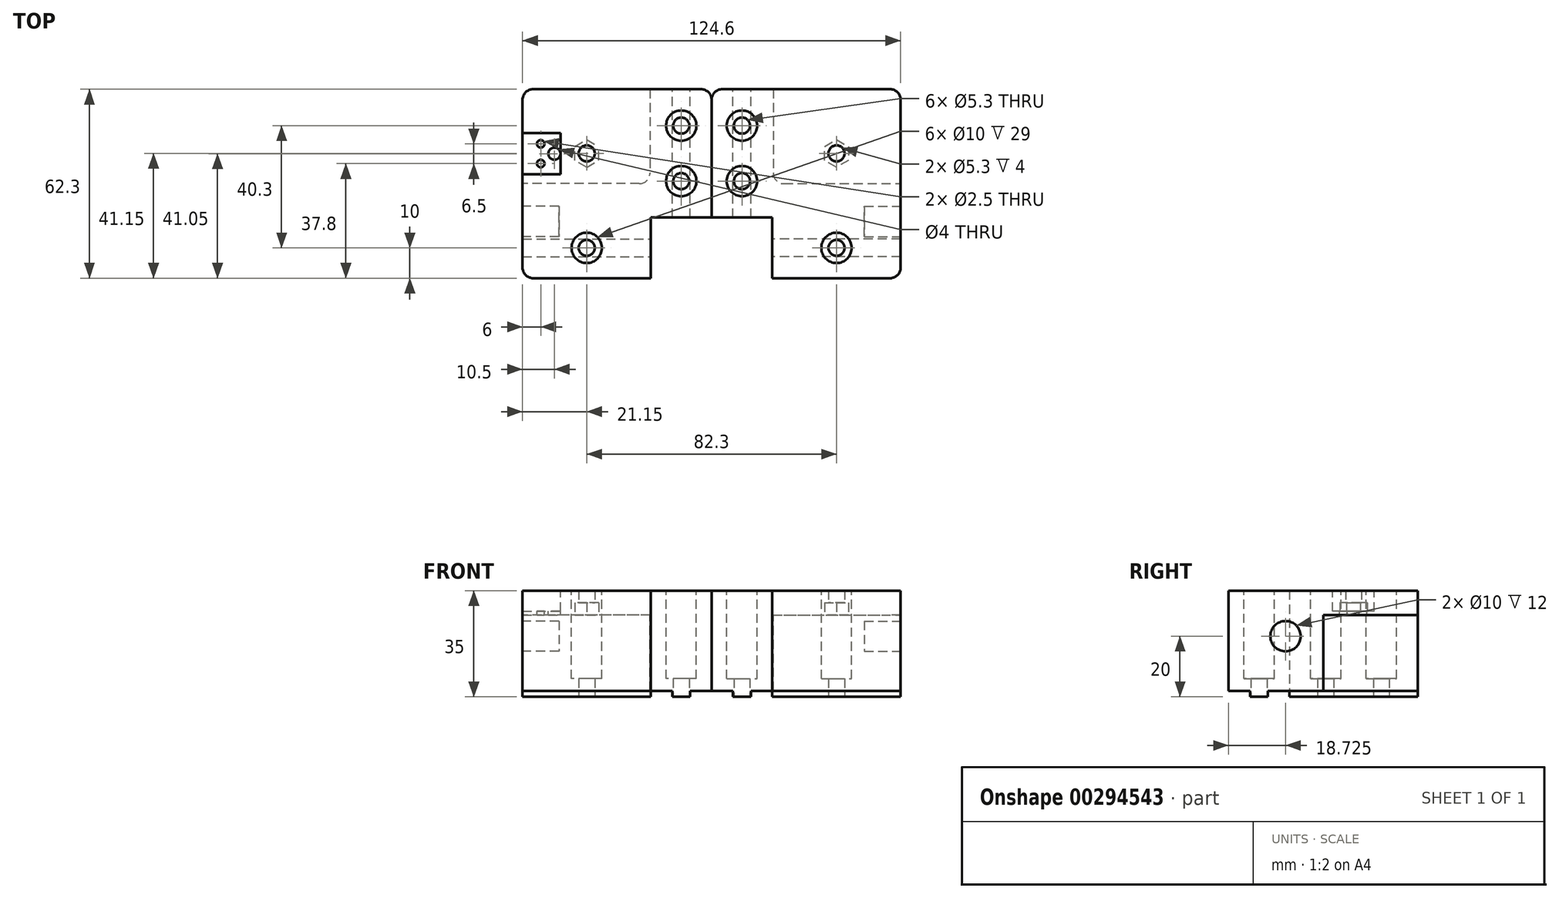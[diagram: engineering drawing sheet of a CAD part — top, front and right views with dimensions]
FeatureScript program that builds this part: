
annotation { "Feature Type Name" : "Feature", "Feature Type Description" : "" }
export const myFeature = defineFeature(function(context is Context, id is Id, definition is map)
    precondition{}
    {
        {
            var Q0;
            Q0=qCreatedBy(makeId("Top.planeOp"),FACE);
            var sketch = newSketch(context, id + "F0", { "sketchPlane" : qUnion([Q0])});
            skLineSegment(sketch, "E0.bottom", {"start": v(-21.15, 35) * mm, "end": v(41.15, 35) * mm});
            skLineSegment(sketch, "E0.top", {"start": v(-21.15, -27.3) * mm, "end": v(21.15, -27.3) * mm});
            skLineSegment(sketch, "E0.left", {"start": v(-21.15, 35) * mm, "end": v(-21.15, -27.3) * mm});
            skLineSegment(sketch, "E0.right", {"start": v(41.15, 35) * mm, "end": v(41.15, -7.3) * mm});
            skLineSegment(sketch, "E1.top", {"start": v(41.15, -7.3) * mm, "end": v(21.15, -7.3) * mm});
            skLineSegment(sketch, "E1.right", {"start": v(21.15, -27.3) * mm, "end": v(21.15, -7.3) * mm});
            skCircle(sketch, "E2", {"center": v(31.15, 23) * mm, "radius": 2.65 * mm});
            skCircle(sketch, "E3", {"center": v(31.15, 4.7) * mm, "radius": 2.65 * mm});
            skCircle(sketch, "E4", {"center": v(0, -17.3) * mm, "radius": 2.65 * mm});
            skPoint(sketch, "E4.centerSnap0", {"position": v(0, -27.3) * mm});
            skCircle(sketch, "E5", {"center": v(0, 13.85) * mm, "radius": 2.65 * mm});
            skSolve(sketch);
        }
        {
            var Q0;
            Q0=qSketchRegion(id+"F0",true);
            extrude(context, id + "F1", {"entities" : qUnion([Q0]), "depth" : 33 * mm});
        }
        {
            var Q0;
            Q0=makeQuery(id+"F1.opExtrude","SWEPT_FACE",FACE,{"disambiguationData":[OSD([sQuery(id+"F0.wireOp",EDGE,"E0.left")])]});
            var sketch = newSketch(context, id + "F2", { "sketchPlane" : qUnion([Q0])});
            skCircle(sketch, "E6", {"center": v(8.58, 18) * mm, "radius": 5 * mm});
            skSolve(sketch);
        }
        {
            var Q0;
            Q0=qSketchRegion(id+"F2",true);
            extrude(context, id + "F3", {"entities" : qUnion([Q0]), "operationType" : NewBodyOperationType.REMOVE, "oppositeDirection" : true, "depth" : 12 * mm});
        }
        {
            var Q0;
            Q0=makeQuery(id+"F1.opExtrude","CAP_FACE",FACE,{"disambiguationData":[OSD([sQuery(id+"F0.wireOp",EDGE,"E0.bottom"),sQuery(id+"F0.wireOp",EDGE,"E0.top"),sQuery(id+"F0.wireOp",EDGE,"E0.left"),sQuery(id+"F0.wireOp",EDGE,"E0.right"),sQuery(id+"F0.wireOp",EDGE,"E1.top"),sQuery(id+"F0.wireOp",EDGE,"E1.right"),sQuery(id+"F0.wireOp",EDGE,"E2"),sQuery(id+"F0.wireOp",EDGE,"E3"),sQuery(id+"F0.wireOp",EDGE,"YSbFCtBf-OZUa-blBg-jqSk-ddDIdjAn90QF"),sQuery(id+"F0.wireOp",EDGE,"E4"),sQuery(id+"F0.wireOp",EDGE,"E5")])],"isStart":true});
            var sketch = newSketch(context, id + "F4", { "sketchPlane" : qUnion([Q0])});
            skCircle(sketch, "E7.0", {"center": v(0, -13.85) * mm, "radius": 2.65 * mm, "construction": true});
            skCircle(sketch, "E8", {"center": v(0, -13.85) * mm, "radius": 3.95 * mm, "construction": true});
            skLineSegment(sketch, "E9", {"start": v(0, -20.58) * mm, "end": v(0, -4.16) * mm, "construction": true});
            skLineSegment(sketch, "E10", {"start": v(-6.74, -13.85) * mm, "end": v(6.1, -13.85) * mm, "construction": true});
            skLineSegment(sketch, "E11", {"start": v(-3.95, -16.13) * mm, "end": v(-3.95, -11.57) * mm});
            skLineSegment(sketch, "E12", {"start": v(-3.95, -11.57) * mm, "end": v(0, -9.29) * mm});
            skLineSegment(sketch, "E13", {"start": v(3.95, -16.13) * mm, "end": v(0, -18.41) * mm});
            skLineSegment(sketch, "E14", {"start": v(0, -18.41) * mm, "end": v(-3.95, -16.13) * mm});
            skLineSegment(sketch, "E15", {"start": v(3.95, -16.13) * mm, "end": v(3.95, -11.57) * mm});
            skLineSegment(sketch, "E16", {"start": v(3.95, -11.57) * mm, "end": v(0, -9.29) * mm});
            skSolve(sketch);
        }
        {
            var Q0;
            Q0=qSketchRegion(id+"F4",true);
            extrude(context, id + "F5", {"entities" : qUnion([Q0]), "operationType" : NewBodyOperationType.REMOVE, "oppositeDirection" : true, "depth" : 29 * mm});
        }
        {
            var Q0;
            Q0=makeQuery(id+"F1.opExtrude","CAP_FACE",FACE,{"disambiguationData":[OSD([sQuery(id+"F0.wireOp",EDGE,"E0.bottom"),sQuery(id+"F0.wireOp",EDGE,"E0.top"),sQuery(id+"F0.wireOp",EDGE,"E0.left"),sQuery(id+"F0.wireOp",EDGE,"E0.right"),sQuery(id+"F0.wireOp",EDGE,"E1.top"),sQuery(id+"F0.wireOp",EDGE,"E1.right"),sQuery(id+"F0.wireOp",EDGE,"E2"),sQuery(id+"F0.wireOp",EDGE,"E3"),sQuery(id+"F0.wireOp",EDGE,"YSbFCtBf-OZUa-blBg-jqSk-ddDIdjAn90QF"),sQuery(id+"F0.wireOp",EDGE,"E4"),sQuery(id+"F0.wireOp",EDGE,"E5")])],"isStart":false});
            var sketch = newSketch(context, id + "F6", { "sketchPlane" : qUnion([Q0])});
            skCircle(sketch, "E17.0", {"center": v(31.15, 23) * mm, "radius": 2.65 * mm, "construction": true});
            skCircle(sketch, "E18.0", {"center": v(31.15, 4.7) * mm, "radius": 2.65 * mm, "construction": true});
            skCircle(sketch, "E19.0", {"center": v(0, -17.3) * mm, "radius": 2.65 * mm, "construction": true});
            skCircle(sketch, "E20", {"center": v(31.15, 23) * mm, "radius": 5 * mm});
            skCircle(sketch, "E21", {"center": v(31.15, 4.7) * mm, "radius": 5 * mm});
            skCircle(sketch, "E22", {"center": v(0, -17.3) * mm, "radius": 5 * mm});
            skSolve(sketch);
        }
        {
            var Q0;
            Q0=qSketchRegion(id+"F6",true);
            extrude(context, id + "F7", {"entities" : qUnion([Q0]), "operationType" : NewBodyOperationType.REMOVE, "oppositeDirection" : true, "depth" : 29 * mm});
        }
        {
            var Q0;
            Q0=makeQuery(id+"F1.opExtrude","CAP_FACE",FACE,{"disambiguationData":[OSD([sQuery(id+"F0.wireOp",EDGE,"E0.bottom"),sQuery(id+"F0.wireOp",EDGE,"E0.top"),sQuery(id+"F0.wireOp",EDGE,"E0.left"),sQuery(id+"F0.wireOp",EDGE,"E0.right"),sQuery(id+"F0.wireOp",EDGE,"E1.top"),sQuery(id+"F0.wireOp",EDGE,"E1.right"),sQuery(id+"F0.wireOp",EDGE,"E2"),sQuery(id+"F0.wireOp",EDGE,"E3"),sQuery(id+"F0.wireOp",EDGE,"YSbFCtBf-OZUa-blBg-jqSk-ddDIdjAn90QF"),sQuery(id+"F0.wireOp",EDGE,"E4"),sQuery(id+"F0.wireOp",EDGE,"E5")])],"isStart":true});
            var sketch = newSketch(context, id + "F8", { "sketchPlane" : qUnion([Q0])});
            skLineSegment(sketch, "E23.bottom", {"start": v(28.2, 7.3) * mm, "end": v(34.1, 7.3) * mm});
            skLineSegment(sketch, "E23.top", {"start": v(28.2, -35) * mm, "end": v(34.1, -35) * mm});
            skLineSegment(sketch, "E23.left", {"start": v(28.2, 7.3) * mm, "end": v(28.2, -13.57) * mm});
            skLineSegment(sketch, "E23.right", {"start": v(34.1, 7.3) * mm, "end": v(34.1, -13.57) * mm});
            skCircle(sketch, "E24.0", {"center": v(31.15, -4.7) * mm, "radius": 2.65 * mm});
            skCircle(sketch, "E25.0", {"center": v(31.15, -23) * mm, "radius": 2.65 * mm});
            skLineSegment(sketch, "E26.trimOffspring", {"start": v(28.2, -13.57) * mm, "end": v(28.2, -35) * mm});
            skLineSegment(sketch, "E27.trimOffspring", {"start": v(34.1, -13.57) * mm, "end": v(34.1, -35) * mm});
            skLineSegment(sketch, "E28.bottom", {"start": v(-21.15, 20.25) * mm, "end": v(21.15, 20.25) * mm});
            skLineSegment(sketch, "E28.top", {"start": v(-21.15, 14.35) * mm, "end": v(21.15, 14.35) * mm});
            skLineSegment(sketch, "E28.left", {"start": v(-21.15, 20.25) * mm, "end": v(-21.15, 14.35) * mm});
            skLineSegment(sketch, "E28.right", {"start": v(21.15, 20.25) * mm, "end": v(21.15, 14.35) * mm});
            skCircle(sketch, "E29.0", {"center": v(0, 17.3) * mm, "radius": 2.65 * mm});
            skSolve(sketch);
        }
        {
            var Q0;
            Q0=qSketchRegion(id+"F8",true);
            extrude(context, id + "F9", {"entities" : qUnion([Q0]), "operationType" : NewBodyOperationType.ADD, "depth" : 2 * mm});
        }
        {
            var Q0;
            Q0=makeQuery(id+"F1.opExtrude","SWEPT_EDGE",EDGE,{"disambiguationData":[OSD([sQuery(id+"F0.wireOp",EDGE,"E0.top"),sQuery(id+"F0.wireOp",EDGE,"E0.left")])]});
            var Q1;
            Q1=makeQuery(id+"F1.opExtrude","SWEPT_EDGE",EDGE,{"disambiguationData":[OSD([sQuery(id+"F0.wireOp",EDGE,"E0.bottom"),sQuery(id+"F0.wireOp",EDGE,"E0.left")])]});
            var Q2;
            Q2=makeQuery(id+"F1.opExtrude","SWEPT_EDGE",EDGE,{"disambiguationData":[OSD([sQuery(id+"F0.wireOp",EDGE,"E0.bottom"),sQuery(id+"F0.wireOp",EDGE,"E0.right")])]});
            fillet(context, id + "F10", {"entities" : qUnion([Q0, Q1, Q2]), "radius" : 3.5 * mm, "tangentPropagation" : true, "allowEdgeOverflow" : false});
        }
        {
            var Q0;
            Q0=makeQuery(id+"F9.boolean.opBoolean","MERGE",FACE,{"derivedFrom":[makeQuery(id+"F1.opExtrude","SWEPT_FACE",FACE,{"disambiguationData":[OSD([sQuery(id+"F0.wireOp",EDGE,"E0.left")])]}),makeQuery(id+"F9.opExtrude","SWEPT_FACE",FACE,{"disambiguationData":[OSD([sQuery(id+"F8.wireOp",EDGE,"E28.left")])]})]});
            var sketch = newSketch(context, id + "F11", { "sketchPlane" : qUnion([Q0])});
            skPoint(sketch, "E30.oppositeSnap0", {"position": v(-3.85, 33) * mm});
            skLineSegment(sketch, "E30.bottom", {"start": v(-35, 0) * mm, "end": v(-3.85, 0) * mm});
            skLineSegment(sketch, "E30.top", {"start": v(-35, 25) * mm, "end": v(-3.85, 25) * mm});
            skLineSegment(sketch, "E30.left", {"start": v(-35, 0) * mm, "end": v(-35, 25) * mm});
            skLineSegment(sketch, "E30.right", {"start": v(-3.85, 0) * mm, "end": v(-3.85, 25) * mm});
            skSolve(sketch);
        }
        {
            var Q0;
            Q0=qSketchRegion(id+"F11",true);
            extrude(context, id + "F12", {"entities" : qUnion([Q0]), "operationType" : NewBodyOperationType.REMOVE, "oppositeDirection" : true, "depth" : 42 * mm});
        }
        {
            var Q0;
            Q0=makeQuery(id+"F12.boolean.opBoolean","COPY",EDGE,{"derivedFrom":makeQuery(id+"F12.opExtrude","CAP_EDGE",EDGE,{"disambiguationData":[OSD([sQuery(id+"F11.wireOp",EDGE,"E30.right")])],"isStart":true})});
            var Q1;
            Q1=makeQuery(id+"F12.boolean.opBoolean","COPY",EDGE,{"derivedFrom":makeQuery(id+"F12.opExtrude","CAP_EDGE",EDGE,{"disambiguationData":[OSD([sQuery(id+"F11.wireOp",EDGE,"E30.right")])],"isStart":false})});
            var Q2;
            Q2=makeQuery(id+"F12.boolean.opBoolean","COPY",EDGE,{"derivedFrom":makeQuery(id+"F12.opExtrude","CAP_EDGE",EDGE,{"disambiguationData":[OSD([sQuery(id+"F11.wireOp",EDGE,"E30.left")])],"isStart":false})});
            fillet(context, id + "F13", {"entities" : qUnion([Q0, Q1, Q2]), "radius" : 3.5 * mm, "tangentPropagation" : true, "allowEdgeOverflow" : false});
        }
        {
            var Q0;
            Q0=makeQuery(id+"F1.opExtrude","SWEPT_BODY",BODY,{"disambiguationData":[OSD([sQuery(id+"F0.wireOp",EDGE,"E0.bottom"),sQuery(id+"F0.wireOp",EDGE,"E0.top"),sQuery(id+"F0.wireOp",EDGE,"E0.left"),sQuery(id+"F0.wireOp",EDGE,"E0.right"),sQuery(id+"F0.wireOp",EDGE,"E1.top"),sQuery(id+"F0.wireOp",EDGE,"E1.right"),sQuery(id+"F0.wireOp",EDGE,"E2"),sQuery(id+"F0.wireOp",EDGE,"E3"),sQuery(id+"F0.wireOp",EDGE,"YSbFCtBf-OZUa-blBg-jqSk-ddDIdjAn90QF"),sQuery(id+"F0.wireOp",EDGE,"E4"),sQuery(id+"F0.wireOp",EDGE,"E5")])]});
            var Q1;
            Q1=makeQuery(id+"F1.opExtrude","SWEPT_FACE",FACE,{"disambiguationData":[OSD([sQuery(id+"F0.wireOp",EDGE,"E0.right")])]});
            mirror(context, id + "F14", {"entities" : qUnion([Q0]), "mirrorPlane" : qUnion([Q1])});
        }
        {
            var Q0;
            Q0=makeQuery(id+"F1.opExtrude","CAP_FACE",FACE,{"disambiguationData":[OSD([sQuery(id+"F0.wireOp",EDGE,"E0.bottom"),sQuery(id+"F0.wireOp",EDGE,"E0.top"),sQuery(id+"F0.wireOp",EDGE,"E0.left"),sQuery(id+"F0.wireOp",EDGE,"E0.right"),sQuery(id+"F0.wireOp",EDGE,"E1.top"),sQuery(id+"F0.wireOp",EDGE,"E1.right"),sQuery(id+"F0.wireOp",EDGE,"E2"),sQuery(id+"F0.wireOp",EDGE,"E3"),sQuery(id+"F0.wireOp",EDGE,"E4"),sQuery(id+"F0.wireOp",EDGE,"E5")])],"isStart":false});
            var sketch = newSketch(context, id + "F15", { "sketchPlane" : qUnion([Q0])});
            skLineSegment(sketch, "E31.bottom", {"start": v(-21.15, 20.6) * mm, "end": v(-13.65, 20.6) * mm});
            skLineSegment(sketch, "E31.top", {"start": v(-21.15, 6.9) * mm, "end": v(-13.65, 6.9) * mm});
            skLineSegment(sketch, "E31.left", {"start": v(-21.15, 20.6) * mm, "end": v(-21.15, 6.9) * mm});
            skLineSegment(sketch, "E31.right", {"start": v(-13.65, 20.6) * mm, "end": v(-13.65, 6.9) * mm});
            skLineSegment(sketch, "E32.bottom", {"start": v(-13.65, 20.6) * mm, "end": v(-8.65, 20.6) * mm});
            skLineSegment(sketch, "E32.top", {"start": v(-13.65, 6.9) * mm, "end": v(-8.65, 6.9) * mm});
            skLineSegment(sketch, "E32.left", {"start": v(-13.65, 20.6) * mm, "end": v(-13.65, 6.9) * mm, "construction": true});
            skLineSegment(sketch, "E32.right", {"start": v(-8.65, 20.6) * mm, "end": v(-8.65, 6.9) * mm});
            skSolve(sketch);
        }
        {
            var Q0;
            Q0=qSketchRegion(id+"F15",true);
            extrude(context, id + "F16", {"entities" : qUnion([Q0]), "operationType" : NewBodyOperationType.REMOVE, "oppositeDirection" : true, "depth" : 6.8 * mm});
        }
        {
            var Q0;
            Q0=makeQuery(id+"F16.boolean.opBoolean","COPY",FACE,{"derivedFrom":makeQuery(id+"F16.opExtrude","CAP_FACE",FACE,{"disambiguationData":[OSD([sQuery(id+"F15.wireOp",EDGE,"E31.bottom"),sQuery(id+"F15.wireOp",EDGE,"E31.top"),sQuery(id+"F15.wireOp",EDGE,"E31.left"),sQuery(id+"F15.wireOp",EDGE,"E31.right")])],"isStart":false})});
            var sketch = newSketch(context, id + "F17", { "sketchPlane" : qUnion([Q0])});
            skCircle(sketch, "E33", {"center": v(-15.15, 17) * mm, "radius": 1.25 * mm});
            skCircle(sketch, "E34", {"center": v(-15.15, 10.5) * mm, "radius": 1.25 * mm});
            skSolve(sketch);
        }
        {
            var Q0;
            Q0=qSketchRegion(id+"F17",true);
            extrude(context, id + "F18", {"entities" : qUnion([Q0]), "operationType" : NewBodyOperationType.REMOVE, "oppositeDirection" : true, "depth" : 8 * mm});
        }
        {
            var Q0;
            Q0=makeQuery(id+"F16.boolean.opBoolean","COPY",FACE,{"derivedFrom":makeQuery(id+"F16.opExtrude","CAP_FACE",FACE,{"disambiguationData":[OSD([sQuery(id+"F15.wireOp",EDGE,"E31.bottom"),sQuery(id+"F15.wireOp",EDGE,"E31.top"),sQuery(id+"F15.wireOp",EDGE,"E31.left"),sQuery(id+"F15.wireOp",EDGE,"E32.bottom"),sQuery(id+"F15.wireOp",EDGE,"E32.top"),sQuery(id+"F15.wireOp",EDGE,"E32.right")])],"isStart":false})});
            var sketch = newSketch(context, id + "F19", { "sketchPlane" : qUnion([Q0])});
            skCircle(sketch, "E35", {"center": v(-10.65, 13.75) * mm, "radius": 2 * mm});
            skPoint(sketch, "E35.centerSnap0", {"position": v(-8.65, 13.75) * mm});
            skSolve(sketch);
        }
        {
            var Q0;
            Q0=qSketchRegion(id+"F19",true);
            extrude(context, id + "F20", {"entities" : qUnion([Q0]), "operationType" : NewBodyOperationType.REMOVE, "oppositeDirection" : true, "depth" : 30 * mm});
        }
    });
